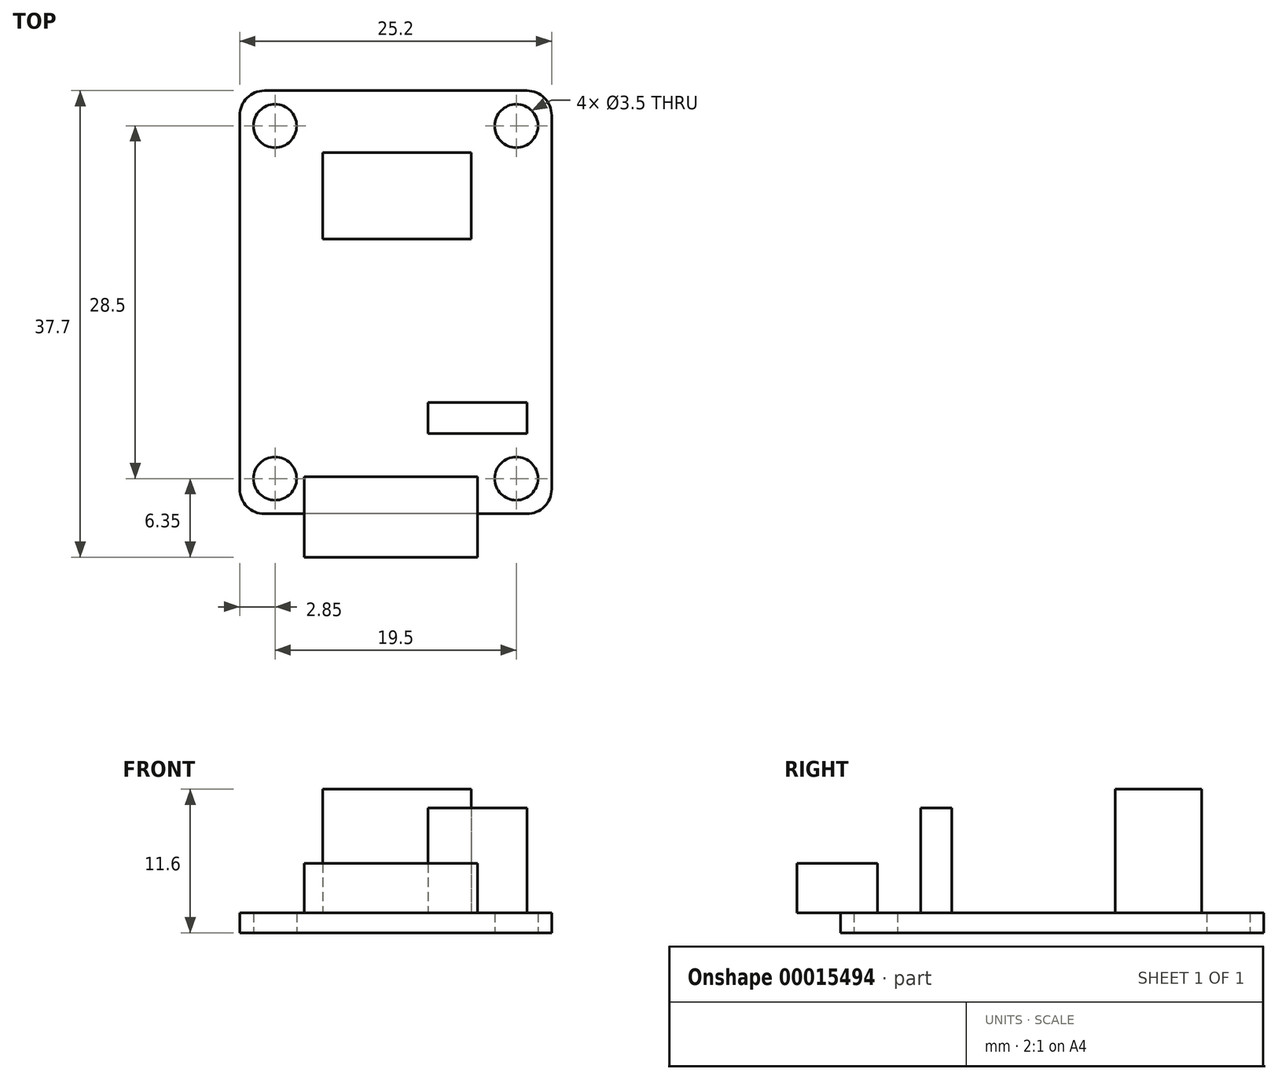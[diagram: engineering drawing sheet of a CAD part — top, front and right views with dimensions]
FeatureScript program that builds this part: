
annotation { "Feature Type Name" : "Feature", "Feature Type Description" : "" }
export const myFeature = defineFeature(function(context is Context, id is Id, definition is map)
    precondition{}
    {
        {
            var Q0;
            Q0=qCreatedBy(makeId("Top.planeOp"),FACE);
            var sketch = newSketch(context, id + "F0", { "sketchPlane" : qUnion([Q0])});
            skLineSegment(sketch, "E0.rect.bottom", {"start": v(12.6, 17.1) * mm, "end": v(-12.6, 17.1) * mm});
            skLineSegment(sketch, "E0.rect.top", {"start": v(12.6, -17.1) * mm, "end": v(-12.6, -17.1) * mm});
            skLineSegment(sketch, "E0.rect.left", {"start": v(12.6, 17.1) * mm, "end": v(12.6, -17.1) * mm});
            skLineSegment(sketch, "E0.rect.right", {"start": v(-12.6, 17.1) * mm, "end": v(-12.6, -17.1) * mm});
            skPoint(sketch, "E0.rect.middle", {"position": v(0, 0) * mm});
            skSolve(sketch);
        }
        {
            var Q0;
            Q0 = qSketchRegion(id + "F0", true);
            extrude(context, id + "F1", {"entities" : qUnion([Q0]), "depth" : 1.6 * mm});
        }
        {
            var Q0;
            Q0=qCreatedBy(makeId("Top.planeOp"),FACE);
            var sketch = newSketch(context, id + "F2", { "sketchPlane" : qUnion([Q0])});
            skLineSegment(sketch, "E1.rect.bottom", {"start": v(9.75, 14.25) * mm, "end": v(-9.75, 14.25) * mm, "construction": true});
            skLineSegment(sketch, "E1.rect.top", {"start": v(9.75, -14.25) * mm, "end": v(-9.75, -14.25) * mm, "construction": true});
            skLineSegment(sketch, "E1.rect.left", {"start": v(9.75, 14.25) * mm, "end": v(9.75, -14.25) * mm, "construction": true});
            skLineSegment(sketch, "E1.rect.right", {"start": v(-9.75, 14.25) * mm, "end": v(-9.75, -14.25) * mm, "construction": true});
            skPoint(sketch, "E1.rect.middle", {"position": v(0, 0) * mm});
            skCircle(sketch, "E2", {"center": v(-9.75, 14.25) * mm, "radius": 1.75 * mm});
            skCircle(sketch, "E3", {"center": v(-9.75, -14.25) * mm, "radius": 1.75 * mm});
            skCircle(sketch, "E4", {"center": v(9.75, -14.25) * mm, "radius": 1.75 * mm});
            skCircle(sketch, "E5", {"center": v(9.75, 14.25) * mm, "radius": 1.75 * mm});
            skSolve(sketch);
        }
        {
            var Q0;
            Q0 = qSketchRegion(id + "F2", true);
            extrude(context, id + "F3", {"entities" : qUnion([Q0]), "operationType" : NewBodyOperationType.REMOVE, "endBound" : BoundingType.UP_TO_NEXT, "depth" : 25 * mm});
        }
        {
            var Q0;
            Q0=makeQuery(id+"F1.opExtrude","SWEPT_EDGE",EDGE,{"disambiguationData":[OSD([sQuery(id+"F0.wireOp",EDGE,"E0.rect.top"),sQuery(id+"F0.wireOp",EDGE,"E0.rect.right")])]});
            var Q1;
            Q1=makeQuery(id+"F1.opExtrude","SWEPT_EDGE",EDGE,{"disambiguationData":[OSD([sQuery(id+"F0.wireOp",EDGE,"E0.rect.top"),sQuery(id+"F0.wireOp",EDGE,"E0.rect.left")])]});
            var Q2;
            Q2=makeQuery(id+"F1.opExtrude","SWEPT_EDGE",EDGE,{"disambiguationData":[OSD([sQuery(id+"F0.wireOp",EDGE,"E0.rect.bottom"),sQuery(id+"F0.wireOp",EDGE,"E0.rect.right")])]});
            var Q3;
            Q3=makeQuery(id+"F1.opExtrude","SWEPT_EDGE",EDGE,{"disambiguationData":[OSD([sQuery(id+"F0.wireOp",EDGE,"E0.rect.bottom"),sQuery(id+"F0.wireOp",EDGE,"E0.rect.left")])]});
            fillet(context, id + "F4", {"entities" : qUnion([Q0, Q1, Q2, Q3]), "radius" : 2 * mm, "tangentPropagation" : true, "allowEdgeOverflow" : false});
        }
        {
            var Q0;
            Q0=makeQuery(id+"F1.opExtrude","CAP_FACE",FACE,{"disambiguationData":[OSD([sQuery(id+"F0.wireOp",EDGE,"E0.rect.bottom"),sQuery(id+"F0.wireOp",EDGE,"E0.rect.top"),sQuery(id+"F0.wireOp",EDGE,"E0.rect.left"),sQuery(id+"F0.wireOp",EDGE,"E0.rect.right")])],"isStart":false});
            var sketch = newSketch(context, id + "F5", { "sketchPlane" : qUnion([Q0])});
            skLineSegment(sketch, "E6.bottom", {"start": v(-5.9, 5.1) * mm, "end": v(6.1, 5.1) * mm});
            skLineSegment(sketch, "E6.top", {"start": v(-5.9, 12.1) * mm, "end": v(6.1, 12.1) * mm});
            skLineSegment(sketch, "E6.left", {"start": v(-5.9, 5.1) * mm, "end": v(-5.9, 12.1) * mm});
            skLineSegment(sketch, "E6.right", {"start": v(6.1, 5.1) * mm, "end": v(6.1, 12.1) * mm});
            skSolve(sketch);
        }
        {
            var Q0;
            Q0 = qSketchRegion(id + "F5", true);
            extrude(context, id + "F6", {"entities" : qUnion([Q0]), "operationType" : NewBodyOperationType.ADD, "depth" : 10 * mm});
        }
        {
            var Q0;
            Q0=makeQuery(id+"F1.opExtrude","CAP_FACE",FACE,{"disambiguationData":[OSD([sQuery(id+"F0.wireOp",EDGE,"E0.rect.bottom"),sQuery(id+"F0.wireOp",EDGE,"E0.rect.top"),sQuery(id+"F0.wireOp",EDGE,"E0.rect.left"),sQuery(id+"F0.wireOp",EDGE,"E0.rect.right")])],"isStart":false});
            var sketch = newSketch(context, id + "F7", { "sketchPlane" : qUnion([Q0])});
            skLineSegment(sketch, "E7.bottom", {"start": v(2.6, -8.1) * mm, "end": v(10.6, -8.1) * mm});
            skLineSegment(sketch, "E7.top", {"start": v(2.6, -10.6) * mm, "end": v(10.6, -10.6) * mm});
            skLineSegment(sketch, "E7.left", {"start": v(2.6, -8.1) * mm, "end": v(2.6, -10.6) * mm});
            skLineSegment(sketch, "E7.right", {"start": v(10.6, -8.1) * mm, "end": v(10.6, -10.6) * mm});
            skSolve(sketch);
        }
        {
            var Q0;
            Q0 = qSketchRegion(id + "F7", true);
            extrude(context, id + "F8", {"entities" : qUnion([Q0]), "operationType" : NewBodyOperationType.ADD, "depth" : 8.5 * mm});
        }
        {
            var Q0;
            Q0=makeQuery(id+"F1.opExtrude","CAP_FACE",FACE,{"disambiguationData":[OSD([sQuery(id+"F0.wireOp",EDGE,"E0.rect.bottom"),sQuery(id+"F0.wireOp",EDGE,"E0.rect.top"),sQuery(id+"F0.wireOp",EDGE,"E0.rect.left"),sQuery(id+"F0.wireOp",EDGE,"E0.rect.right")])],"isStart":false});
            var sketch = newSketch(context, id + "F9", { "sketchPlane" : qUnion([Q0])});
            skLineSegment(sketch, "E8.bottom", {"start": v(-7.4, -14.1) * mm, "end": v(6.6, -14.1) * mm});
            skLineSegment(sketch, "E8.top", {"start": v(-7.4, -20.6) * mm, "end": v(6.6, -20.6) * mm});
            skLineSegment(sketch, "E8.left", {"start": v(-7.4, -14.1) * mm, "end": v(-7.4, -20.6) * mm});
            skLineSegment(sketch, "E8.right", {"start": v(6.6, -14.1) * mm, "end": v(6.6, -20.6) * mm});
            skSolve(sketch);
        }
        {
            var Q0;
            {var subQ0=sQuery(id+"F9.wireOp",EDGE,"E8.top");Q0=makeQuery(id+"F9.imprint","IMPRINT",FACE,{"disambiguationData":[TD([[makeQuery(id+"F9.imprint","IMPRINT",EDGE,{"derivedFrom":subQ0}),1.0]])]});}
            var Q1;
            {var subQ0=sQuery(id+"F9.wireOp",EDGE,"E8.bottom");Q1=makeQuery(id+"F9.imprint","IMPRINT",FACE,{"disambiguationData":[TD([[makeQuery(id+"F9.imprint","IMPRINT",EDGE,{"derivedFrom":subQ0}),-1.0]])]});}
            extrude(context, id + "F10", {"entities" : qUnion([Q0, Q1]), "operationType" : NewBodyOperationType.ADD, "depth" : 4 * mm});
        }
    });
